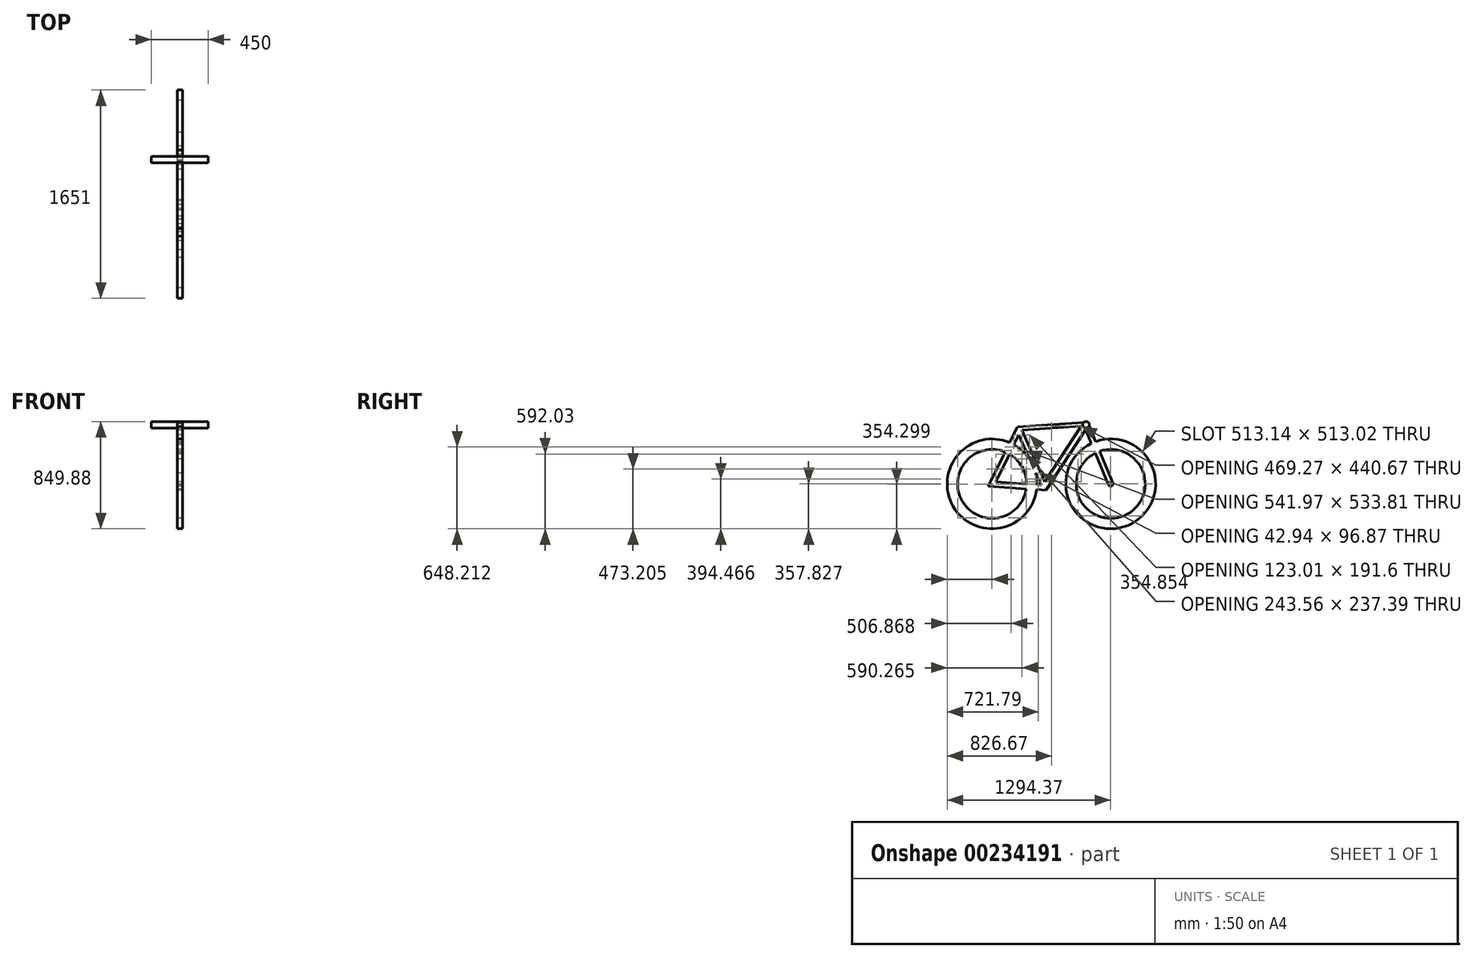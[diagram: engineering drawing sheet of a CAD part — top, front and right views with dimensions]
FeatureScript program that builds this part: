
annotation { "Feature Type Name" : "Feature", "Feature Type Description" : "" }
export const myFeature = defineFeature(function(context is Context, id is Id, definition is map)
    precondition{}
    {
        {
            var Q0;
            Q0=qCreatedBy(makeId("Right.planeOp"),FACE);
            var sketch = newSketch(context, id + "F0", { "sketchPlane" : qUnion([Q0])});
            skCircle(sketch, "E0", {"center": v(-417.96, 30.9) * mm, "radius": 349.25 * mm});
            skCircle(sketch, "E1", {"center": v(521.84, 30.9) * mm, "radius": 349.25 * mm});
            skLineSegment(sketch, "E2", {"start": v(-417.96, 30.9) * mm, "end": v(-205.88, 464.41) * mm});
            skLineSegment(sketch, "E3", {"start": v(-205.88, 464.41) * mm, "end": v(0, 0) * mm});
            skLineSegment(sketch, "E4", {"start": v(0, 0) * mm, "end": v(-417.96, 30.9) * mm});
            skLineSegment(sketch, "E5", {"start": v(0, 0) * mm, "end": v(326.35, 499.79) * mm});
            skLineSegment(sketch, "E6", {"start": v(326.35, 499.79) * mm, "end": v(-205.88, 464.41) * mm});
            skLineSegment(sketch, "E7", {"start": v(326.35, 499.79) * mm, "end": v(521.84, 30.9) * mm});
            skLineSegment(sketch, "E8", {"start": v(2167.03, -318.34) * mm, "end": v(-1513.43, -318.34) * mm});
            skSolve(sketch);
        }
        {
            var Q0;
            Q0=qCreatedBy(makeId("Right.planeOp"),FACE);
            var sketch = newSketch(context, id + "F1", { "sketchPlane" : qUnion([Q0])});
            skCircle(sketch, "E9.0", {"center": v(-417.96, 30.9) * mm, "radius": 355.6 * mm});
            skCircle(sketch, "E10.0", {"center": v(-417.96, 30.9) * mm, "radius": 273.05 * mm});
            skCircle(sketch, "E11.0", {"center": v(521.84, 30.9) * mm, "radius": 355.6 * mm});
            skCircle(sketch, "E12.0", {"center": v(521.84, 30.9) * mm, "radius": 273.05 * mm});
            skSolve(sketch);
        }
        {
            var Q0;
            Q0=qCreatedBy(makeId("Right.planeOp"),FACE);
            var sketch = newSketch(context, id + "F2", { "sketchPlane" : qUnion([Q0])});
            skLineSegment(sketch, "E13.0", {"start": v(-205.88, 464.41) * mm, "end": v(0, 0) * mm, "construction": true});
            skLineSegment(sketch, "E13.1", {"start": v(-417.96, 30.9) * mm, "end": v(-205.88, 464.41) * mm, "construction": true});
            skLineSegment(sketch, "E13.2", {"start": v(0, 0) * mm, "end": v(-417.96, 30.9) * mm, "construction": true});
            skLineSegment(sketch, "E13.3", {"start": v(326.35, 499.79) * mm, "end": v(-205.88, 464.41) * mm, "construction": true});
            skLineSegment(sketch, "E13.4", {"start": v(0, 0) * mm, "end": v(326.35, 499.79) * mm, "construction": true});
            skLineSegment(sketch, "E13.5", {"start": v(326.35, 499.79) * mm, "end": v(521.84, 30.9) * mm, "construction": true});
            skLineSegment(sketch, "E14.0", {"start": v(338.69, 519.7) * mm, "end": v(539.42, 38.24) * mm});
            skLineSegment(sketch, "E14.1", {"start": v(338.69, 519.7) * mm, "end": v(-218.14, 482.69) * mm});
            skLineSegment(sketch, "E14.2", {"start": v(-447.44, 13.99) * mm, "end": v(-218.14, 482.69) * mm});
            skLineSegment(sketch, "E14.3", {"start": v(9.8, -19.83) * mm, "end": v(-447.44, 13.99) * mm});
            skLineSegment(sketch, "E15", {"start": v(9.8, -19.83) * mm, "end": v(322.62, 459.23) * mm});
            skLineSegment(sketch, "E16", {"start": v(322.62, 459.23) * mm, "end": v(504.26, 23.58) * mm});
            skLineSegment(sketch, "E17", {"start": v(-181.53, 456.48) * mm, "end": v(0, 47) * mm});
            skLineSegment(sketch, "E18", {"start": v(0, 47) * mm, "end": v(287.75, 487.67) * mm});
            skLineSegment(sketch, "E19", {"start": v(287.75, 487.67) * mm, "end": v(-181.53, 456.48) * mm});
            skLineSegment(sketch, "E20", {"start": v(-206.73, 419.32) * mm, "end": v(-388.47, 47.83) * mm});
            skLineSegment(sketch, "E21", {"start": v(-388.47, 47.83) * mm, "end": v(-30.3, 21.34) * mm});
            skLineSegment(sketch, "E22", {"start": v(-30.3, 21.34) * mm, "end": v(-206.73, 419.32) * mm});
            skArc(sketch, "E23", {"start": v(504.26, 23.58) * mm, "mid": v(529.17, 13.33) * mm, "end": v(539.42, 38.24) * mm});
            skSolve(sketch);
        }
        {
            var Q0;
            Q0 = qSketchRegion(id + "F2", true);
            extrude(context, id + "F3", {"entities" : qUnion([Q0]), "endBound" : BoundingType.SYMMETRIC, "depth" : 40 * mm});
        }
        {
            var Q0;
            Q0 = qSketchRegion(id + "F1", true);
            extrude(context, id + "F4", {"entities" : qUnion([Q0]), "operationType" : NewBodyOperationType.ADD, "endBound" : BoundingType.SYMMETRIC, "depth" : 40 * mm});
        }
        {
            var Q0;
            Q0=qCreatedBy(makeId("Right.planeOp"),FACE);
            var sketch = newSketch(context, id + "F5", { "sketchPlane" : qUnion([Q0])});
            skCircle(sketch, "E24", {"center": v(326.35, 499.79) * mm, "radius": 25.4 * mm});
            skSolve(sketch);
        }
        {
            var Q0;
            Q0 = qSketchRegion(id + "F5", true);
            extrude(context, id + "F6", {"entities" : qUnion([Q0]), "operationType" : NewBodyOperationType.ADD, "endBound" : BoundingType.SYMMETRIC, "depth" : 450 * mm, "offsetDistance" : 25.4 * mm});
        }
    });
